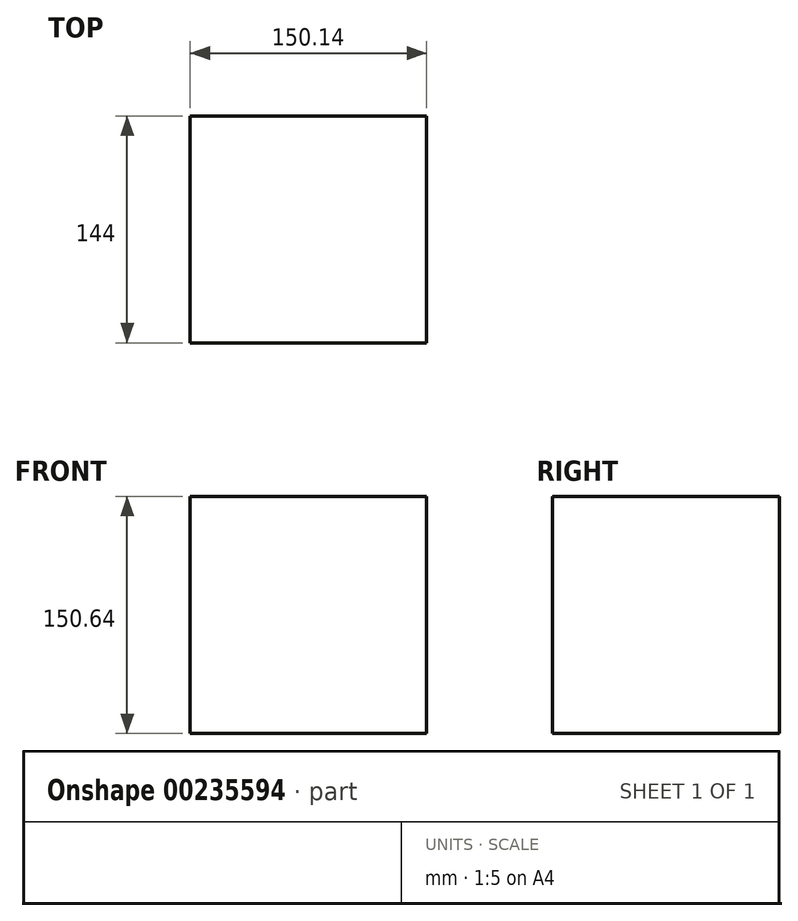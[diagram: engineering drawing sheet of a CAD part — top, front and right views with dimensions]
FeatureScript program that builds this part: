
annotation { "Feature Type Name" : "Feature", "Feature Type Description" : "" }
export const myFeature = defineFeature(function(context is Context, id is Id, definition is map)
    precondition{}
    {
        {
            var Q0;
            Q0=qCreatedBy(makeId("Front.planeOp"),FACE);
            var sketch = newSketch(context, id + "F0", { "sketchPlane" : qUnion([Q0])});
            skLineSegment(sketch, "E0.bottom", {"start": v(-5.89, -74.82) * mm, "end": v(5.64, -74.82) * mm});
            skLineSegment(sketch, "E0.top", {"start": v(-5.89, -55.69) * mm, "end": v(5.64, -55.69) * mm});
            skLineSegment(sketch, "E0.left", {"start": v(-5.89, -74.82) * mm, "end": v(-5.89, -55.69) * mm});
            skLineSegment(sketch, "E0.right", {"start": v(5.64, -74.82) * mm, "end": v(5.64, -55.69) * mm});
            skSolve(sketch);
        }
        {
            var Q0;
            Q0 = qSketchRegion(id + "F0", true);
            extrude(context, id + "F1", {"entities" : qUnion([Q0]), "depth" : 25 * mm});
        }
        {
            var Q0;
            Q0=qCreatedBy(makeId("Front.planeOp"),FACE);
            var sketch = newSketch(context, id + "F2", { "sketchPlane" : qUnion([Q0])});
            skLineSegment(sketch, "E1.bottom", {"start": v(-75.07, 75.32) * mm, "end": v(75.07, 75.32) * mm});
            skLineSegment(sketch, "E1.top", {"start": v(-75.07, -75.32) * mm, "end": v(75.07, -75.32) * mm});
            skLineSegment(sketch, "E1.left", {"start": v(-75.07, 75.32) * mm, "end": v(-75.07, -75.32) * mm});
            skLineSegment(sketch, "E1.right", {"start": v(75.07, 75.32) * mm, "end": v(75.07, -75.32) * mm});
            skSolve(sketch);
        }
        {
            var Q0;
            Q0=makeQuery(id+"F2.imprint","IMPRINT",FACE,{"disambiguationData":[TD([[makeQuery(id+"F2.imprint","IMPRINT",EDGE,{"derivedFrom":sQuery(id+"F2.wireOp",EDGE,"E1.bottom")}),-1.0]])]});
            extrude(context, id + "F3", {"entities" : qUnion([Q0]), "operationType" : NewBodyOperationType.ADD, "depth" : 72 * mm});
        }
        {
            var Q0;
            Q0=makeQuery(id+"F3.boolean.opBoolean","MERGE",FACE,{"derivedFrom":[makeQuery(id+"F1.opExtrude","CAP_FACE",FACE,{"disambiguationData":[OSD([sQuery(id+"F0.wireOp",EDGE,"E0.bottom"),sQuery(id+"F0.wireOp",EDGE,"E0.top"),sQuery(id+"F0.wireOp",EDGE,"E0.left"),sQuery(id+"F0.wireOp",EDGE,"E0.right")])],"isStart":true}),makeQuery(id+"F3.opExtrude","CAP_FACE",FACE,{"disambiguationData":[OSD([sQuery(id+"F2.wireOp",EDGE,"E1.bottom"),sQuery(id+"F2.wireOp",EDGE,"E1.top"),sQuery(id+"F2.wireOp",EDGE,"E1.left"),sQuery(id+"F2.wireOp",EDGE,"E1.right")])],"isStart":true})]});
            extrude(context, id + "F4", {"entities" : qUnion([Q0]), "operationType" : NewBodyOperationType.ADD, "depth" : 72 * mm});
        }
    });
